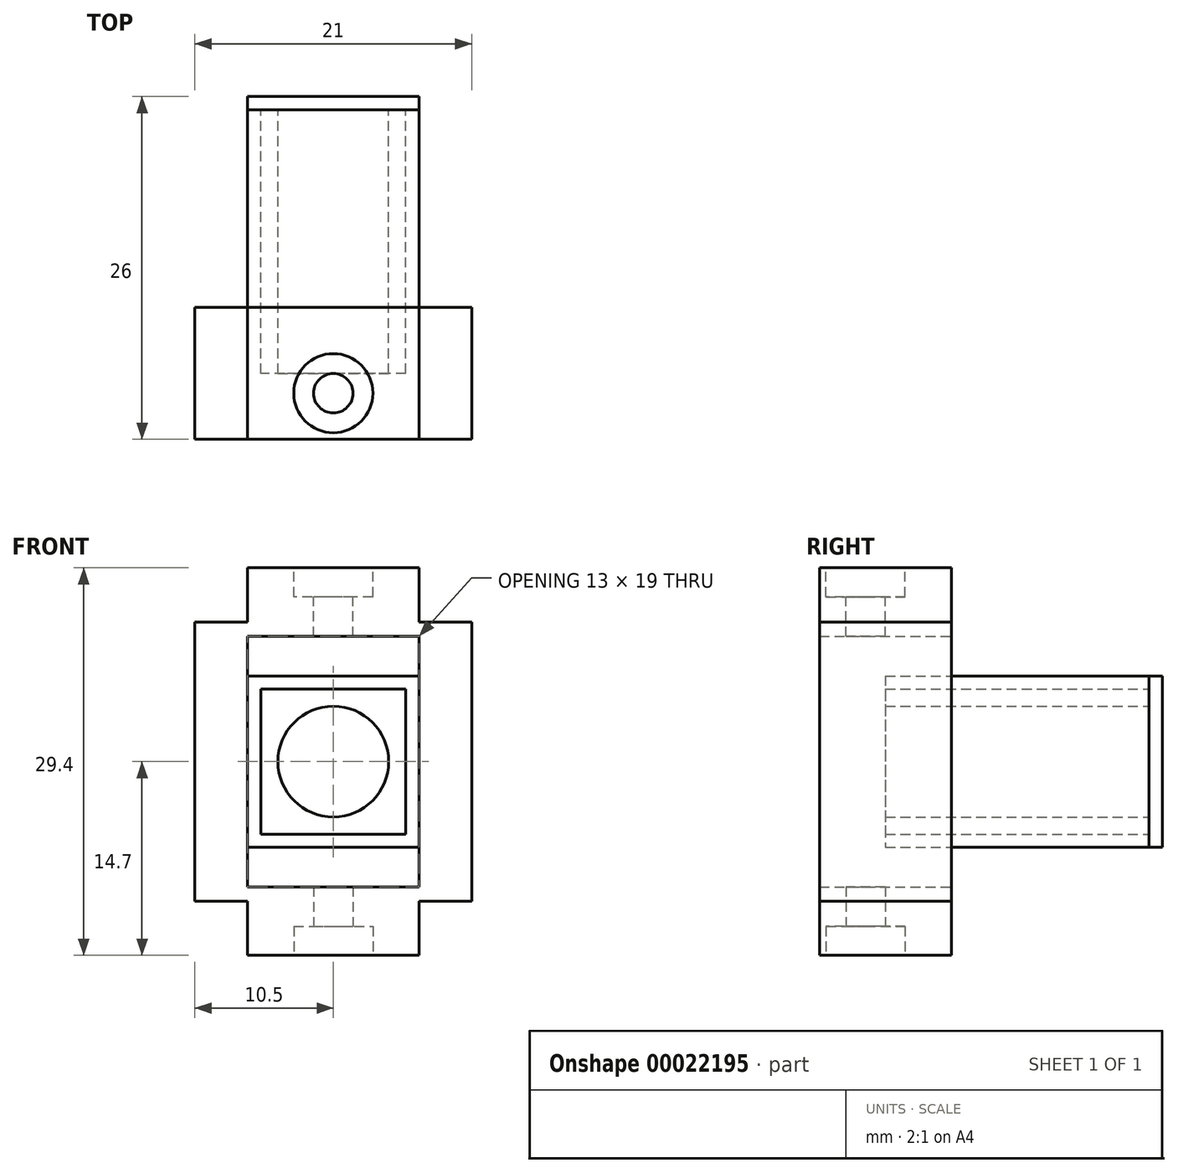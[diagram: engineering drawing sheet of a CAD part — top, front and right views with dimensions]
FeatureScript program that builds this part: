
annotation { "Feature Type Name" : "Feature", "Feature Type Description" : "" }
export const myFeature = defineFeature(function(context is Context, id is Id, definition is map)
    precondition{}
    {
        {
            var Q0;
            Q0=qCreatedBy(makeId("Front.planeOp"),FACE);
            var sketch = newSketch(context, id + "F0", { "sketchPlane" : qUnion([Q0])});
            skLineSegment(sketch, "E0.rect.bottom", {"start": v(5.5, 5.5) * mm, "end": v(-5.5, 5.5) * mm});
            skLineSegment(sketch, "E0.rect.top", {"start": v(5.5, -5.5) * mm, "end": v(-5.5, -5.5) * mm});
            skLineSegment(sketch, "E0.rect.left", {"start": v(5.5, 5.5) * mm, "end": v(5.5, -5.5) * mm});
            skLineSegment(sketch, "E0.rect.right", {"start": v(-5.5, 5.5) * mm, "end": v(-5.5, -5.5) * mm});
            skPoint(sketch, "E0.rect.middle", {"position": v(0, 0) * mm});
            skLineSegment(sketch, "E1.rect.bottom", {"start": v(6.5, 6.5) * mm, "end": v(-6.5, 6.5) * mm});
            skLineSegment(sketch, "E1.rect.top", {"start": v(6.5, -6.5) * mm, "end": v(-6.5, -6.5) * mm});
            skLineSegment(sketch, "E1.rect.left", {"start": v(6.5, 6.5) * mm, "end": v(6.5, -6.5) * mm});
            skLineSegment(sketch, "E1.rect.right", {"start": v(-6.5, 6.5) * mm, "end": v(-6.5, -6.5) * mm});
            skSolve(sketch);
        }
        {
            var Q0;
            Q0 = qSketchRegion(id + "F0", true);
            extrude(context, id + "F1", {"entities" : qUnion([Q0]), "depth" : 20 * mm});
        }
        {
            var Q0;
            Q0=makeQuery(id+"F1.opExtrude","CAP_FACE",FACE,{"disambiguationData":[OSD([sQuery(id+"F0.wireOp",EDGE,"E0.rect.bottom"),sQuery(id+"F0.wireOp",EDGE,"E0.rect.top"),sQuery(id+"F0.wireOp",EDGE,"E0.rect.left"),sQuery(id+"F0.wireOp",EDGE,"E0.rect.right"),sQuery(id+"F0.wireOp",EDGE,"E1.rect.bottom"),sQuery(id+"F0.wireOp",EDGE,"E1.rect.top"),sQuery(id+"F0.wireOp",EDGE,"E1.rect.left"),sQuery(id+"F0.wireOp",EDGE,"E1.rect.right")])],"isStart":true});
            var sketch = newSketch(context, id + "F2", { "sketchPlane" : qUnion([Q0])});
            skLineSegment(sketch, "E2.rect.bottom", {"start": v(6.5, 6.5) * mm, "end": v(-6.5, 6.5) * mm});
            skLineSegment(sketch, "E2.rect.top", {"start": v(6.5, -6.5) * mm, "end": v(-6.5, -6.5) * mm});
            skLineSegment(sketch, "E2.rect.left", {"start": v(6.5, 6.5) * mm, "end": v(6.5, -6.5) * mm});
            skLineSegment(sketch, "E2.rect.right", {"start": v(-6.5, 6.5) * mm, "end": v(-6.5, -6.5) * mm});
            skPoint(sketch, "E2.rect.middle", {"position": v(0, 0) * mm});
            skSolve(sketch);
        }
        {
            var Q0;
            Q0=makeQuery(id+"F2.imprint","IMPRINT",FACE,{"disambiguationData":[TD([[makeQuery(id+"F2.imprint","IMPRINT",EDGE,{"derivedFrom":makeQuery(id+"F1.opExtrude","CAP_EDGE",EDGE,{"disambiguationData":[OSD([sQuery(id+"F0.wireOp",EDGE,"E0.rect.bottom")])],"isStart":true})}),-1.0]])]});
            var sketch = newSketch(context, id + "F3", { "sketchPlane" : qUnion([Q0])});
            skCircle(sketch, "E3", {"center": v(0, 0) * mm, "radius": 4.2 * mm});
            skSolve(sketch);
        }
        {
            var Q0;
            Q0 = qSketchRegion(id + "F3", true);
            extrude(context, id + "F4", {"entities" : qUnion([Q0]), "oppositeDirection" : true, "depth" : 20 * mm});
        }
        {
            var Q0;
            Q0 = qSketchRegion(id + "F2", true);
            extrude(context, id + "F5", {"entities" : qUnion([Q0]), "depth" : 1 * mm});
        }
        {
            var Q0;
            Q0=makeQuery(id+"F1.opExtrude","CAP_FACE",FACE,{"disambiguationData":[OSD([sQuery(id+"F0.wireOp",EDGE,"E0.rect.bottom"),sQuery(id+"F0.wireOp",EDGE,"E0.rect.top"),sQuery(id+"F0.wireOp",EDGE,"E0.rect.left"),sQuery(id+"F0.wireOp",EDGE,"E0.rect.right"),sQuery(id+"F0.wireOp",EDGE,"E1.rect.bottom"),sQuery(id+"F0.wireOp",EDGE,"E1.rect.top"),sQuery(id+"F0.wireOp",EDGE,"E1.rect.left"),sQuery(id+"F0.wireOp",EDGE,"E1.rect.right")])],"isStart":false});
            var sketch = newSketch(context, id + "F6", { "sketchPlane" : qUnion([Q0])});
            skLineSegment(sketch, "E4.bottom", {"start": v(-6.5, 6.5) * mm, "end": v(6.5, 6.5) * mm});
            skLineSegment(sketch, "E4.top", {"start": v(-6.5, 14.7) * mm, "end": v(6.5, 14.7) * mm});
            skLineSegment(sketch, "E4.left", {"start": v(-6.5, 6.5) * mm, "end": v(-6.5, 14.7) * mm});
            skLineSegment(sketch, "E4.right", {"start": v(6.5, 6.5) * mm, "end": v(6.5, 14.7) * mm});
            skLineSegment(sketch, "E5", {"start": v(-6.5, 6.5) * mm, "end": v(-6.5, 0) * mm});
            skLineSegment(sketch, "E6", {"start": v(6.5, 6.5) * mm, "end": v(6.5, 0) * mm});
            skLineSegment(sketch, "E7.top", {"start": v(-6.5, 10.6) * mm, "end": v(-10.5, 10.6) * mm});
            skLineSegment(sketch, "E7.right", {"start": v(-10.5, 1.87) * mm, "end": v(-10.5, 10.6) * mm});
            skLineSegment(sketch, "E8.top", {"start": v(6.5, 10.6) * mm, "end": v(6.5, 10.6) * mm});
            skLineSegment(sketch, "E8.left", {"start": v(6.5, 10.6) * mm, "end": v(6.5, 10.6) * mm});
            skLineSegment(sketch, "E8.right", {"start": v(6.5, 7.76) * mm, "end": v(6.5, 10.6) * mm});
            skLineSegment(sketch, "E9.bottom", {"start": v(6.5, 10.6) * mm, "end": v(10.5, 10.6) * mm});
            skLineSegment(sketch, "E9.right", {"start": v(10.5, 10.6) * mm, "end": v(10.5, 1.87) * mm});
            skLineSegment(sketch, "E10", {"start": v(-6.5, 0) * mm, "end": v(6.5, 0) * mm, "construction": true});
            skLineSegment(sketch, "E11.MirrorCS", {"start": v(-6.5, -10.6) * mm, "end": v(-10.5, -10.6) * mm});
            skLineSegment(sketch, "E12.MirrorCS", {"start": v(-10.5, -1.87) * mm, "end": v(-10.5, -10.6) * mm});
            skLineSegment(sketch, "E13.MirrorCS", {"start": v(-6.5, -1.87) * mm, "end": v(-6.5, -10.6) * mm});
            skLineSegment(sketch, "E14.MirrorCS", {"start": v(-6.5, -14.7) * mm, "end": v(6.5, -14.7) * mm});
            skLineSegment(sketch, "E15.MirrorCS", {"start": v(-6.5, -6.5) * mm, "end": v(-6.5, -14.7) * mm});
            skLineSegment(sketch, "E16.MirrorCS", {"start": v(-6.5, -6.5) * mm, "end": v(6.5, -6.5) * mm});
            skLineSegment(sketch, "E17.MirrorCS", {"start": v(6.5, -6.5) * mm, "end": v(6.5, -14.7) * mm});
            skLineSegment(sketch, "E18.MirrorCS", {"start": v(6.5, -10.6) * mm, "end": v(10.5, -10.6) * mm});
            skLineSegment(sketch, "E19.MirrorCS", {"start": v(10.5, -10.6) * mm, "end": v(10.5, -1.87) * mm});
            skLineSegment(sketch, "E20", {"start": v(-6.5, 10.6) * mm, "end": v(-6.5, 6.5) * mm});
            skLineSegment(sketch, "E21", {"start": v(6.5, 10.6) * mm, "end": v(6.5, 6.5) * mm});
            skLineSegment(sketch, "E22", {"start": v(-6.5, 9.5) * mm, "end": v(6.5, 9.5) * mm});
            skLineSegment(sketch, "E23", {"start": v(-6.5, 9.5) * mm, "end": v(-6.5, 6.5) * mm});
            skLineSegment(sketch, "E24", {"start": v(-10.5, 1.87) * mm, "end": v(-10.5, -1.87) * mm});
            skLineSegment(sketch, "E25", {"start": v(10.5, 1.87) * mm, "end": v(10.5, -1.87) * mm});
            skLineSegment(sketch, "E26.MirrorCS", {"start": v(-6.5, -9.5) * mm, "end": v(6.5, -9.5) * mm});
            skSolve(sketch);
        }
        {
            var Q0;
            Q0=makeQuery(id+"F6.imprint","IMPRINT",FACE,{"disambiguationData":[TD([[makeQuery(id+"F6.imprint","IMPRINT",EDGE,{"derivedFrom":sQuery(id+"F6.wireOp",EDGE,"E4.top")}),-1.0]])]});
            var Q1;
            {var subQ2=sQuery(id+"F6.wireOp",EDGE,"E5");Q1=makeQuery(id+"F6.imprint","IMPRINT",FACE,{"disambiguationData":[TD([[makeQuery(id+"F6.imprint","IMPRINT",EDGE,{"derivedFrom":subQ2}),-1.0]])]});}
            var Q2;
            {var subQ2=sQuery(id+"F6.wireOp",EDGE,"E6");Q2=makeQuery(id+"F6.imprint","IMPRINT",FACE,{"disambiguationData":[TD([[makeQuery(id+"F6.imprint","IMPRINT",EDGE,{"derivedFrom":subQ2}),1.0]])]});}
            var Q3;
            {var subQ6=sQuery(id+"F6.wireOp",EDGE,"E14.MirrorCS");Q3=makeQuery(id+"F6.imprint","IMPRINT",FACE,{"disambiguationData":[TD([[makeQuery(id+"F6.imprint","IMPRINT",EDGE,{"derivedFrom":subQ6}),1.0]])]});}
            extrude(context, id + "F7", {"entities" : qUnion([Q0, Q1, Q2, Q3]), "endBound" : BoundingType.SYMMETRIC, "depth" : 10 * mm});
        }
        {
            var Q0;
            Q0=makeQuery(id+"F7.opExtrude","SWEPT_FACE",FACE,{"disambiguationData":[OSD([sQuery(id+"F6.wireOp",EDGE,"E4.top")])]});
            var sketch = newSketch(context, id + "F8", { "sketchPlane" : qUnion([Q0])});
            skCircle(sketch, "E27", {"center": v(0, -21.5) * mm, "radius": 3 * mm});
            skLineSegment(sketch, "E28", {"start": v(6.5, -20) * mm, "end": v(-6.5, -20) * mm, "construction": true});
            skLineSegment(sketch, "E29", {"start": v(-6.5, -15) * mm, "end": v(-6.5, -25) * mm});
            skLineSegment(sketch, "E30", {"start": v(6.5, -15) * mm, "end": v(6.5, -25) * mm});
            skLineSegment(sketch, "E31", {"start": v(6.5, -23) * mm, "end": v(6.5, -25) * mm});
            skLineSegment(sketch, "E32", {"start": v(6.5, -24) * mm, "end": v(6.5, -25) * mm});
            skLineSegment(sketch, "E33", {"start": v(6.5, -24.5) * mm, "end": v(-6.5, -24.5) * mm, "construction": true});
            skLineSegment(sketch, "E34", {"start": v(0, -21.5) * mm, "end": v(0, -25) * mm, "construction": true});
            skLineSegment(sketch, "E35", {"start": v(0, -21.5) * mm, "end": v(6.5, -21.5) * mm, "construction": true});
            skLineSegment(sketch, "E36", {"start": v(0, -21.5) * mm, "end": v(-6.5, -21.5) * mm, "construction": true});
            skSolve(sketch);
        }
        {
            var Q0;
            Q0=makeQuery(id+"F8.imprint","IMPRINT",FACE,{"disambiguationData":[TD([[makeQuery(id+"F8.imprint","IMPRINT",EDGE,{"derivedFrom":sQuery(id+"F8.wireOp",EDGE,"E27")}),1.0]])]});
            extrude(context, id + "F9", {"entities" : qUnion([Q0]), "operationType" : NewBodyOperationType.REMOVE, "oppositeDirection" : true, "depth" : 2.2 * mm});
        }
        {
            var Q0;
            Q0=makeQuery(id+"F9.boolean.opBoolean","COPY",FACE,{"derivedFrom":makeQuery(id+"F9.opExtrude","CAP_FACE",FACE,{"disambiguationData":[OSD([sQuery(id+"F8.wireOp",EDGE,"E27")])],"isStart":false})});
            var sketch = newSketch(context, id + "F10", { "sketchPlane" : qUnion([Q0])});
            skCircle(sketch, "E37", {"center": v(0, -21.5) * mm, "radius": 1.5 * mm});
            skSolve(sketch);
        }
        {
            var Q0;
            Q0 = qSketchRegion(id + "F10", true);
            extrude(context, id + "F11", {"entities" : qUnion([Q0]), "operationType" : NewBodyOperationType.REMOVE, "oppositeDirection" : true, "depth" : 3 * mm});
        }
        {
            var Q0;
            Q0=makeQuery(id+"F7.opExtrude","SWEPT_FACE",FACE,{"disambiguationData":[OSD([sQuery(id+"F6.wireOp",EDGE,"E14.MirrorCS")])]});
            var sketch = newSketch(context, id + "F12", { "sketchPlane" : qUnion([Q0])});
            skCircle(sketch, "E38", {"center": v(0, 21.5) * mm, "radius": 3 * mm});
            skLineSegment(sketch, "E39", {"start": v(0, 25) * mm, "end": v(0, 15) * mm, "construction": true});
            skSolve(sketch);
        }
        {
            var Q0;
            Q0 = qSketchRegion(id + "F12", true);
            extrude(context, id + "F13", {"entities" : qUnion([Q0]), "operationType" : NewBodyOperationType.REMOVE, "oppositeDirection" : true, "depth" : 2.2 * mm});
        }
        {
            var Q0;
            Q0=makeQuery(id+"F13.boolean.opBoolean","COPY",FACE,{"derivedFrom":makeQuery(id+"F13.opExtrude","CAP_FACE",FACE,{"disambiguationData":[OSD([sQuery(id+"F12.wireOp",EDGE,"E38")])],"isStart":false})});
            var sketch = newSketch(context, id + "F14", { "sketchPlane" : qUnion([Q0])});
            skCircle(sketch, "E40", {"center": v(0, 21.5) * mm, "radius": 1.5 * mm});
            skSolve(sketch);
        }
        {
            var Q0;
            Q0 = qSketchRegion(id + "F14", true);
            extrude(context, id + "F15", {"entities" : qUnion([Q0]), "operationType" : NewBodyOperationType.REMOVE, "oppositeDirection" : true, "depth" : 3 * mm});
        }
    });
